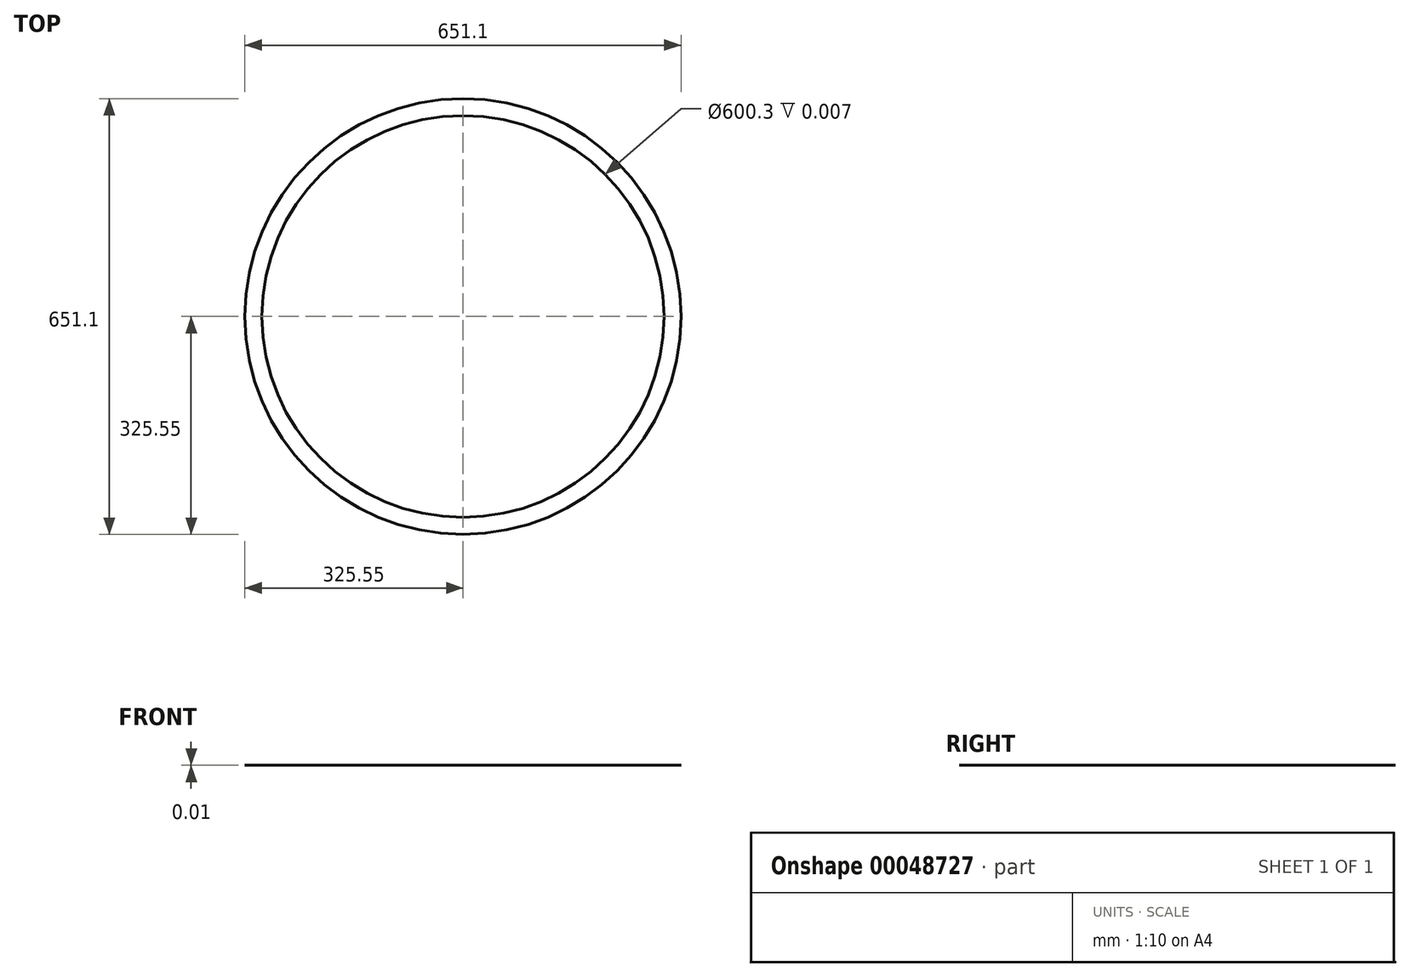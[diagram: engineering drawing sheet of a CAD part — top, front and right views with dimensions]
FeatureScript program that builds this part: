
annotation { "Feature Type Name" : "Feature", "Feature Type Description" : "" }
export const myFeature = defineFeature(function(context is Context, id is Id, definition is map)
    precondition{}
    {
        {
            var Q0;
            Q0=qCreatedBy(makeId("Top.planeOp"),FACE);
            var sketch = newSketch(context, id + "F0", { "sketchPlane" : qUnion([Q0])});
            skCircle(sketch, "E0", {"center": v(0, 0) * mm, "radius": 325.55 * mm});
            skCircle(sketch, "E1", {"center": v(0, 0) * mm, "radius": 300.15 * mm});
            skSolve(sketch);
        }
        {
            var Q0;
            Q0=makeQuery(id+"F0.imprint","IMPRINT",FACE,{"disambiguationData":[TD([[makeQuery(id+"F0.imprint","IMPRINT",EDGE,{"derivedFrom":sQuery(id+"F0.wireOp",EDGE,"E0")}),1.0]])]});
            extrude(context, id + "F1", {"entities" : qUnion([Q0]), "depth" : 3 / 406.4 * mm});
        }
    });
